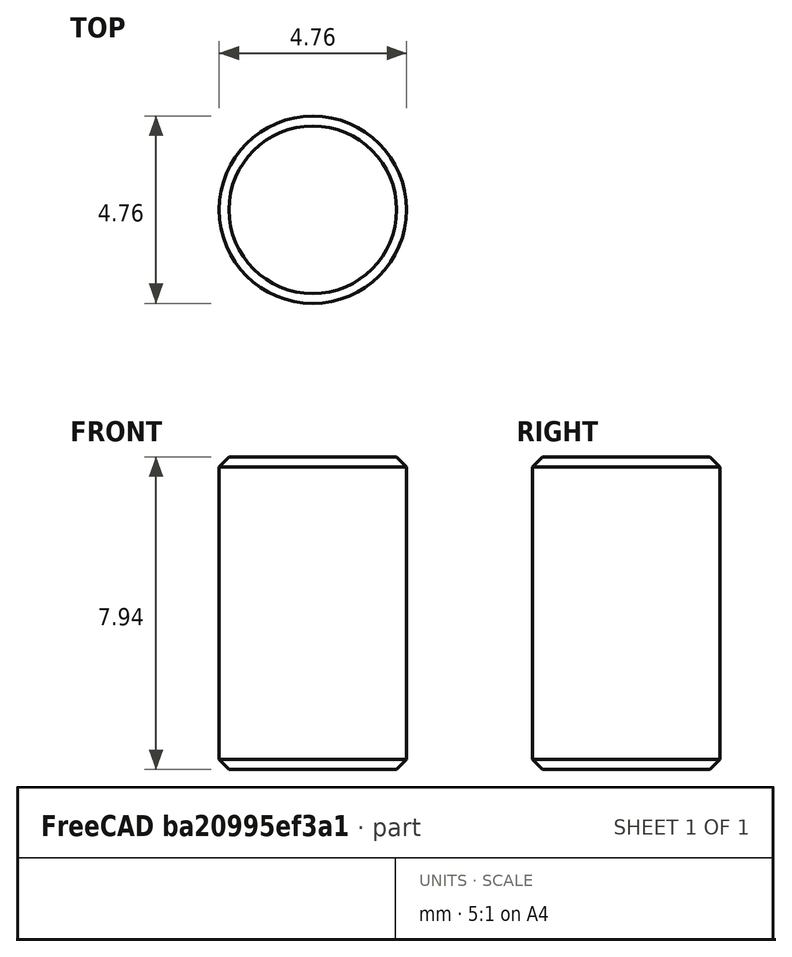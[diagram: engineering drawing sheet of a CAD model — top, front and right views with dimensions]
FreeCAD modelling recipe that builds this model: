
FCSTD DOCUMENT  (FreeCAD 0.21R33668 +26 (Git))
Label: Door Hardware Dowell Pin Small
License: All rights reserved
LicenseURL: http://en.wikipedia.org/wiki/All_rights_reserved
objects: Sketcher::SketchObject×1, PartDesign::Pad×1, PartDesign::Chamfer×1, PartDesign::Body×1
note: 6 computed .brp shape members not serialized (recipe doc carries the construction recipe); baked Part::Feature solids carry a one-line shape summary decoded from their .brp

FEATURE [Sketcher::SketchObject] Sketch
  FullyConstrained = true
  MapMode = 5
  Support = -> [XY_Plane]
  sketch-geometry (1):
    g0: Circle CenterX=0 CenterY=0 CenterZ=0 NormalX=0 NormalY=0 NormalZ=1 AngleXU=0 Radius=2.38
  constraints (2):
    c: Coincident(g0,g-1)
    c: Diameter(g0) = 4.76
FEATURE [PartDesign::Pad] Pad
  Direction = (0,0,1)
  Length = 7.94
  Length2 = 10
  Profile = -> Sketch
  ReferenceAxis = -> Sketch [N_Axis]
  Type = 0
FEATURE [PartDesign::Chamfer] Chamfer
  Angle = 45
  Base = -> Pad [Edge3,Edge2]
  BaseFeature = -> Pad
  ChamferType = 0
  FlipDirection = false
  Size = 0.25
  Size2 = 1
  SupportTransform = false
  UseAllEdges = false
FEATURE [PartDesign::Body] Body
  Group = -> [Sketch,Pad,Chamfer]
  Origin = -> Origin
  Tip = -> Chamfer
